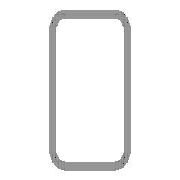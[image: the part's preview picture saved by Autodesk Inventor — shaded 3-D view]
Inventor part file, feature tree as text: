
AUTODESK INVENTOR PART (.ipt)
format: ipt  version: 2025 (Build 290162010, 162A)  size: 133,120 bytes
history: native  units: mm (DEFAULTED — no unit token found)
features: other x4, sketch x1, plane x1
ambient origin geometry x8: Origin, YZ Plane, XZ Plane, XY Plane, X Axis, Y Axis, Z Axis, Center Point
bodies: Solid1 (feature_tree), Body (feature_tree)
feature tree (6):
  parser-record x1  (decoder bookkeeping rows leaked as tree rows — omitted from the tree; the rows remain in map.json)
  other  "Driven Length"
  other  "Start Plane"
  other  "End Plane"
  sketch  "Sketch3"  dims[d3=1500.0mm d4=0.0mm d7=4.0mm d9=40.0mm d11=60.0mm d12=2.0mm d13=-0.0mm d14=1500.0mm d15=20.0mm d16=30.0mm d17=90.0deg d18=1500.0mm]
  plane  "Work Plane3"
